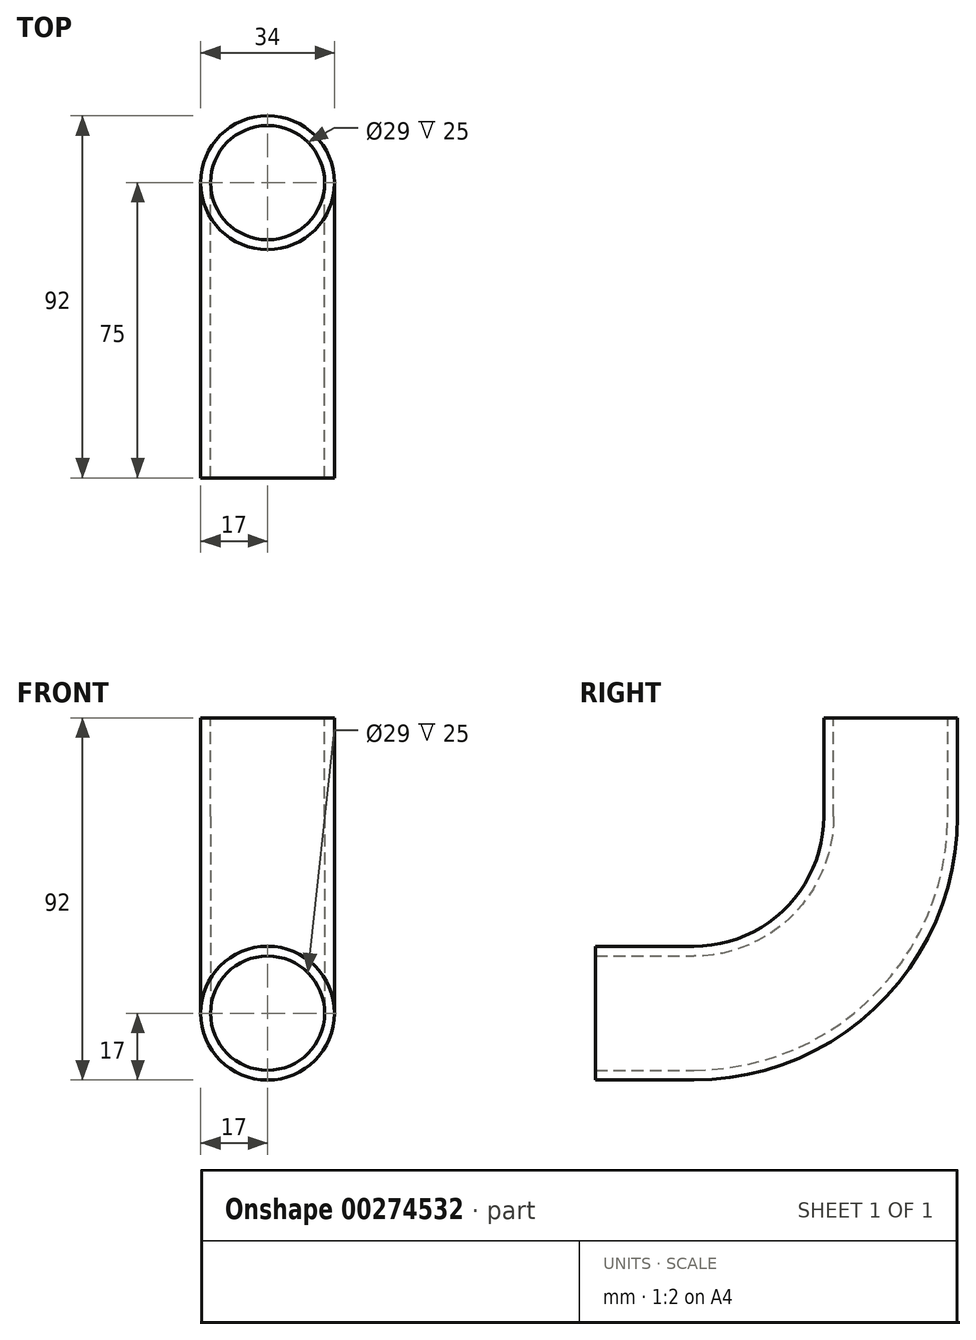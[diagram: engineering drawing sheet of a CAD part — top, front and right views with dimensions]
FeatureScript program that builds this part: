
annotation { "Feature Type Name" : "Feature", "Feature Type Description" : "" }
export const myFeature = defineFeature(function(context is Context, id is Id, definition is map)
    precondition{}
    {
        {
            var Q0;
            Q0=qCreatedBy(makeId("Front.planeOp"),FACE);
            var sketch = newSketch(context, id + "F0", { "sketchPlane" : qUnion([Q0])});
            skCircle(sketch, "E0", {"center": v(0, 0) * mm, "radius": 17 * mm});
            skSolve(sketch);
        }
        {
            var Q0;
            Q0=qCreatedBy(makeId("Right.planeOp"),FACE);
            var sketch = newSketch(context, id + "F1", { "sketchPlane" : qUnion([Q0])});
            skLineSegment(sketch, "E1", {"start": v(0, 0) * mm, "end": v(25, 0) * mm});
            skLineSegment(sketch, "E2", {"start": v(75, 50) * mm, "end": v(75, 75) * mm});
            skPoint(sketch, "E3.visualSharp", {"position": v(75, 0) * mm});
            skArc(sketch, "E3.filletArc", {"start": v(25, 0) * mm, "mid": v(60.36, 14.64) * mm, "end": v(75, 50) * mm});
            skSolve(sketch);
        }
        {
            var Q0;
            Q0=makeQuery(id+"F0.imprint","IMPRINT",FACE,{"disambiguationData":[TD([[makeQuery(id+"F0.imprint","IMPRINT",EDGE,{"derivedFrom":sQuery(id+"F0.wireOp",EDGE,"E0")}),1.0]])]});
            var Q1;
            Q1=sQuery(id+"F1.wireOp",EDGE,"E3.filletArc");
            var Q2;
            Q2=sQuery(id+"F1.wireOp",EDGE,"E2");
            var Q3;
            Q3=sQuery(id+"F1.wireOp",EDGE,"E1");
            sweep(context, id + "F2", {"profiles" : qUnion([Q0]), "path" : qUnion([Q1, Q2, Q3])});
        }
        {
            var Q0;
            Q0=makeQuery(id+"F2.opSweep","CAP_FACE",FACE,{"disambiguationData":[OSD([sQuery(id+"F0.wireOp",EDGE,"E0"),sQuery(id+"F1.wireOp",VERTEX,"E1.start")])],"isStart":true});
            var Q1;
            Q1=makeQuery(id+"F2.opSweep","CAP_FACE",FACE,{"disambiguationData":[OSD([sQuery(id+"F0.wireOp",EDGE,"E0"),sQuery(id+"F1.wireOp",VERTEX,"E2.end")])],"isStart":false});
            shell(context, id + "F3", {"entities" : qUnion([Q0, Q1]), "thickness" : 2.5 * mm});
        }
    });
